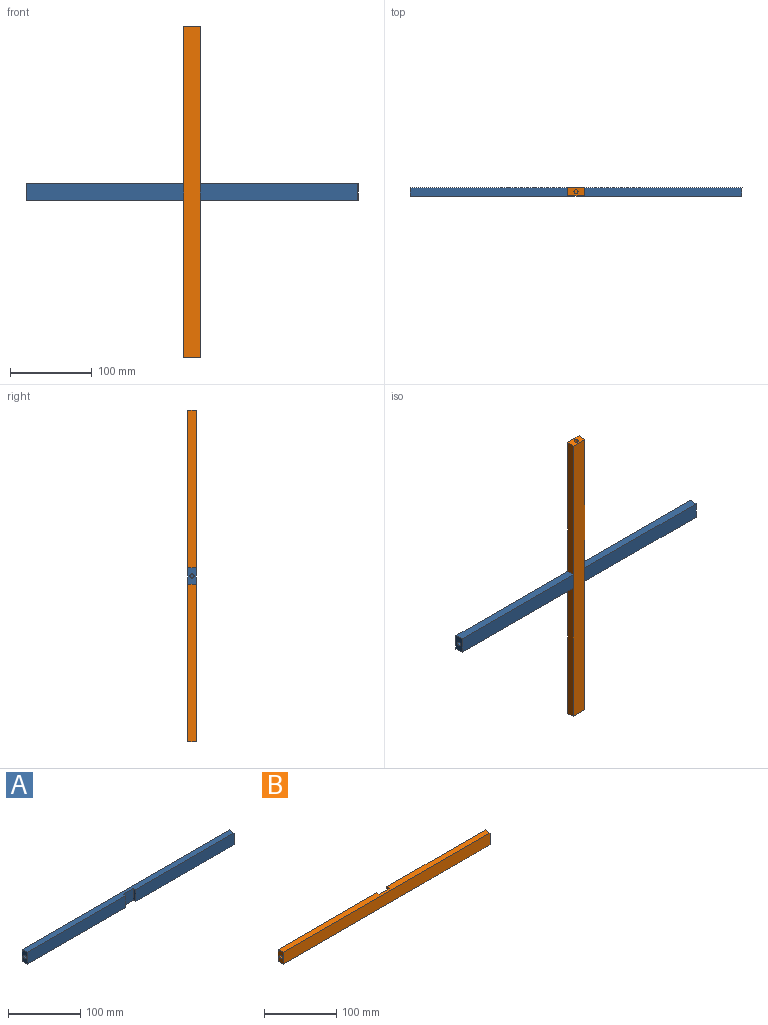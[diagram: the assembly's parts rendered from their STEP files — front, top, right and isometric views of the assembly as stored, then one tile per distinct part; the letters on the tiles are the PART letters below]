
ASSEMBLY  parts=2 mates=1
PART A: 14 faces, bbox 405.1x10.1x20.1 mm
  f0: plane 191.63x20mm, normal (0,-1,0), area 3832.5mm2, adj f1,f2,f6,f8
  f1: plane 405x10mm, normal (0,0,1), area 3941.3mm2, adj f0,f3,f4,f5,f6,f7,f8,f9
  f2: plane 405x10mm, normal (0,0,-1), area 3941.3mm2, adj f0,f3,f4,f5,f6,f7,f8,f9
  f3: plane 191.63x20mm, normal (0,-1,0), area 3832.5mm2, adj f1,f2,f5,f9
  f4: plane 405x20mm, normal (0,1,0), area 8100mm2, adj f1,f2,f8,f9
  f5: plane 20x5mm, normal (1,0,0), area 100mm2, adj f1,f2,f3,f7
  f6: plane 20x5mm, normal (-1,0,0), area 100mm2, adj f0,f1,f2,f7
  f7: plane 20x20mm, normal (0,-1,0), area 400mm2, adj f1,f2,f5,f6
  f8: plane 20.09x10.09mm, normal (1,-0.09,0), area 181.1mm2, adj f0,f1,f2,f4,f11
  f9: plane 20.09x10.09mm, normal (-1,-0.09,0), area 181.1mm2, adj f1,f2,f3,f4,f13
  f10: plane 5x5mm, normal (1,0,0), area 19.6mm2, adj f11
  f11: cylinder r=2.5mm len=5mm, axis (1,0,0), area 71.6mm2, adj f8,f10
  f12: plane 5x5mm, normal (-1,0,0), area 19.6mm2, adj f13
  f13: cylinder r=2.5mm len=5mm, axis (-1,0,0), area 71.6mm2, adj f9,f12
PART B: 14 faces, bbox 405.1x10.1x20.1 mm
  f0: plane 192.5x20mm, normal (0,1,0), area 3850mm2, adj f1,f5,f8,f11
  f1: plane 405x10mm, normal (0,0,1), area 3941.3mm2, adj f0,f4,f6,f7,f8,f11,f12,f13
  f2: cylinder r=2.5mm len=5mm, axis (-1,0,0), area 71.6mm2, adj f3,f4
  f3: plane 5x5mm, normal (-1,0,0), area 19.6mm2, adj f2
  f4: plane 20.09x10.09mm, normal (-1,-0.09,0), area 181.1mm2, adj f1,f2,f5,f6,f7
  f5: plane 405x10mm, normal (0,0,-1), area 3941.3mm2, adj f0,f4,f6,f7,f8,f11,f12,f13
  f6: plane 403.25x20mm, normal (0,-1,0), area 8065mm2, adj f1,f4,f5,f8
  f7: plane 192.5x20mm, normal (0,1,0), area 3850mm2, adj f1,f4,f5,f12
  f8: plane 20.09x10.09mm, normal (1,-0.09,0), area 181.1mm2, adj f0,f1,f5,f6,f10
  f9: plane 5x5mm, normal (1,0,0), area 19.6mm2, adj f10
  f10: cylinder r=2.5mm len=5mm, axis (1,0,0), area 71.6mm2, adj f8,f9
  f11: plane 20x5mm, normal (-1,0,0), area 100mm2, adj f0,f1,f5,f13
  f12: plane 20x5mm, normal (1,0,0), area 100mm2, adj f1,f5,f7,f13
  f13: plane 20x20mm, normal (0,1,0), area 400mm2, adj f1,f5,f11,f12
PLACE A t=(173.64,-32.24,185.47)mm
PLACE B rot(axis=(0,1,0),90deg) t=(173.64,-32.24,185.47)mm
MATE fastened A.f7 <-> B.f13  axis (0,-1,0) through (173.64,-37.24,185.47)mm
